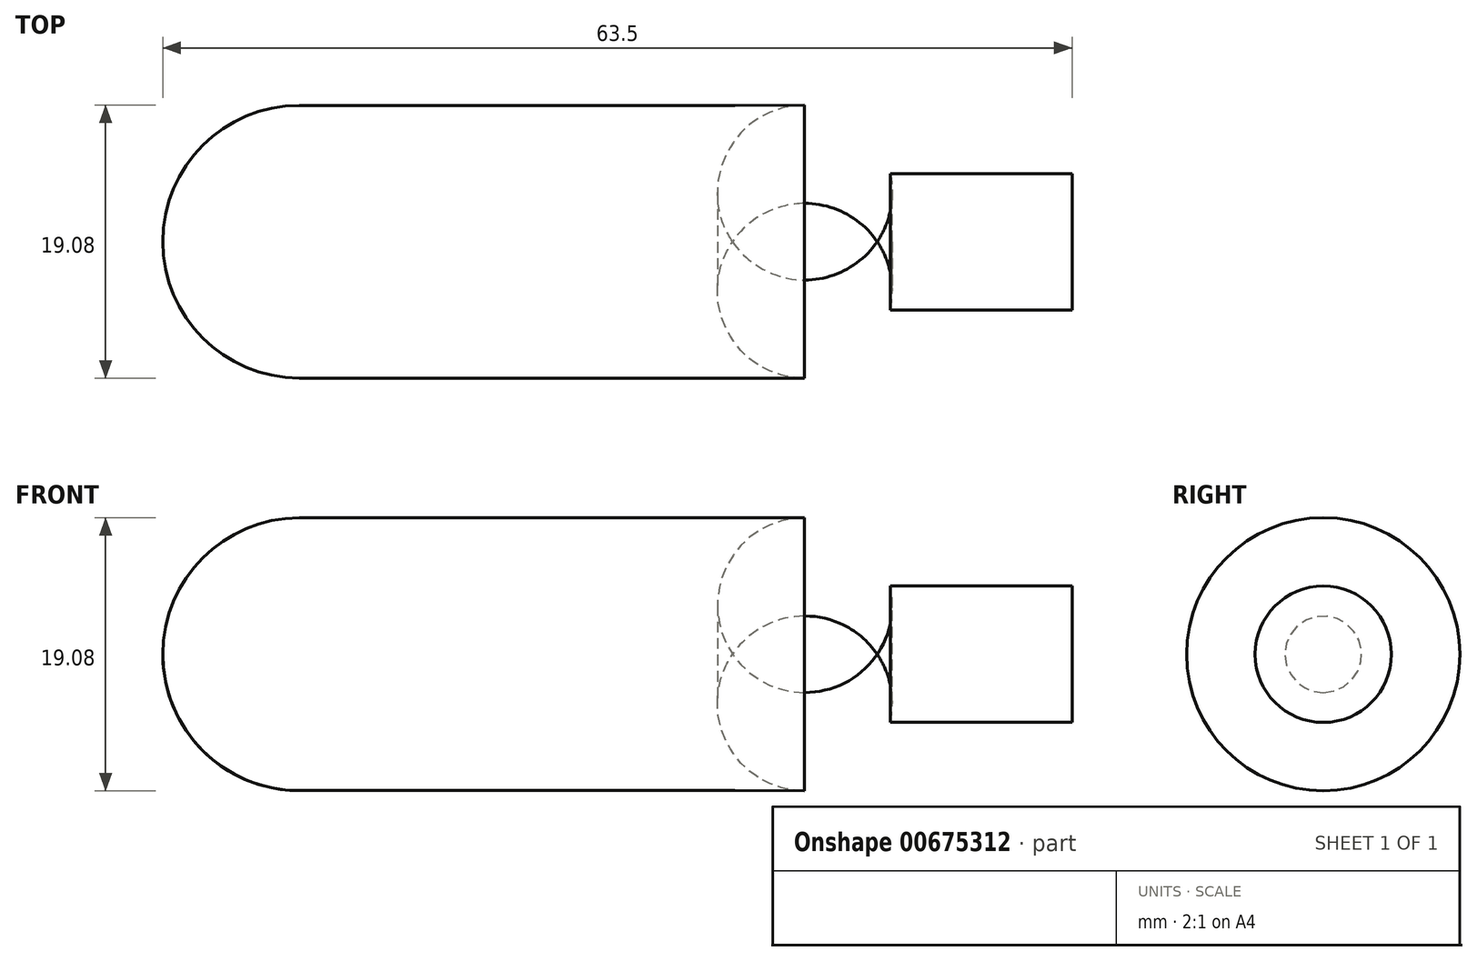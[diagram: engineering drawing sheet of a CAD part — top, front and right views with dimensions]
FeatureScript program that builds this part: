
annotation { "Feature Type Name" : "Feature", "Feature Type Description" : "" }
export const myFeature = defineFeature(function(context is Context, id is Id, definition is map)
    precondition{}
    {
        {
            var Q0;
            Q0=qCreatedBy(makeId("Front.planeOp"),FACE);
            var sketch = newSketch(context, id + "F0", { "sketchPlane" : qUnion([Q0])});
            skLineSegment(sketch, "E0", {"start": v(54.37, 11.85) * mm, "end": v(49.48, 11.84) * mm});
            skLineSegment(sketch, "E1", {"start": v(9.48, 11.84) * mm, "end": v(49.48, 11.84) * mm});
            skArc(sketch, "E2", {"start": v(60.35, 7.08) * mm, "mid": v(58.2, 10.52) * mm, "end": v(54.37, 11.85) * mm});
            skLineSegment(sketch, "E3", {"start": v(60.35, 7.08) * mm, "end": v(73.05, 7.08) * mm});
            skLineSegment(sketch, "E4", {"start": v(9.55, 2.31) * mm, "end": v(73.05, 2.31) * mm});
            skLineSegment(sketch, "E5", {"start": v(9.55, 11.84) * mm, "end": v(9.55, 2.31) * mm});
            skLineSegment(sketch, "E6", {"start": v(73.05, 7.08) * mm, "end": v(73.05, 2.31) * mm});
            skSolve(sketch);
        }
        {
            var Q0;
            {var subQ1=sQuery(id+"F0.wireOp",EDGE,"E0");Q0=makeQuery(id+"F0.imprint","IMPRINT",FACE,{"disambiguationData":[TD([[makeQuery(id+"F0.imprint","IMPRINT",EDGE,{"derivedFrom":subQ1}),1.0]])]});}
            var Q1;
            Q1=sQuery(id+"F0.wireOp",EDGE,"E4");
            revolve(context, id + "F1", {"entities" : qUnion([Q0]), "axis" : qUnion([Q1]), "revolveType" : RevolveType.FULL});
        }
        {
            var Q0;
            Q0=makeQuery(id+"F1.opRevolve","SWEPT_EDGE",EDGE,{"disambiguationData":[OSD([sQuery(id+"F0.wireOp",EDGE,"E1"),sQuery(id+"F0.wireOp",EDGE,"E5")])]});
            fillet(context, id + "F2", {"entities" : qUnion([Q0]), "radius" : 9.52 * mm, "tangentPropagation" : true, "allowEdgeOverflow" : false});
        }
    });
